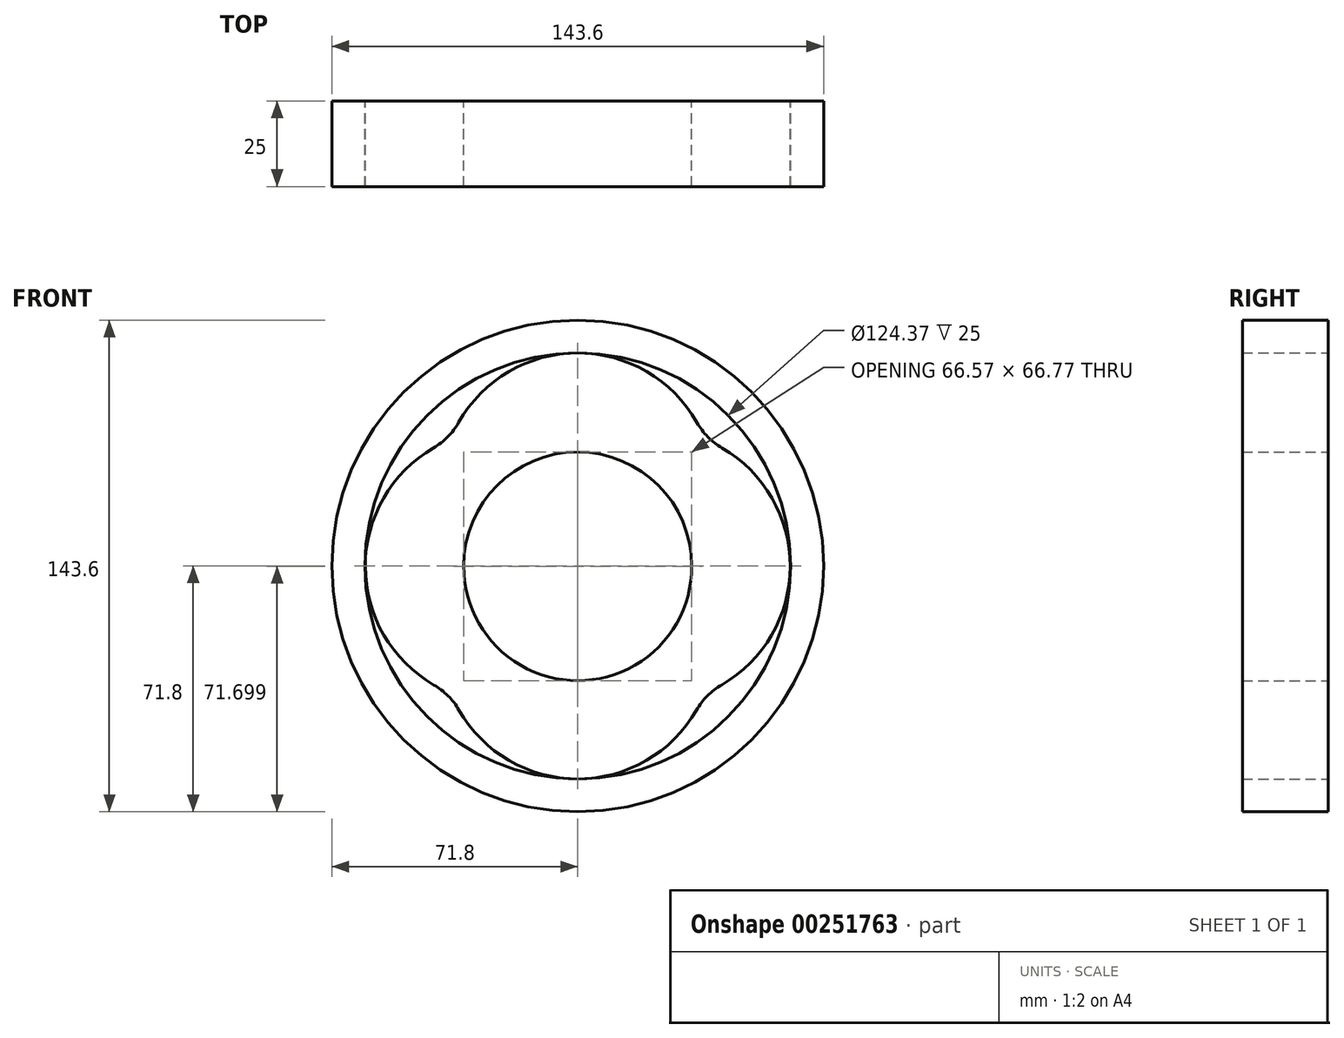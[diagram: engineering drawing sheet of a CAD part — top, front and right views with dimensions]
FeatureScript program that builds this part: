
annotation { "Feature Type Name" : "Feature", "Feature Type Description" : "" }
export const myFeature = defineFeature(function(context is Context, id is Id, definition is map)
    precondition{}
    {
        {
            var Q0;
            Q0=qCreatedBy(makeId("Front.planeOp"),FACE);
            var sketch = newSketch(context, id + "F0", { "sketchPlane" : qUnion([Q0])});
            skArc(sketch, "E0", {"start": v(33.28, 0) * mm, "mid": v(0, 33.28) * mm, "end": v(-33.28, 0) * mm});
            skArc(sketch, "E1", {"start": v(-33.28, 0) * mm, "mid": v(0, -33.49) * mm, "end": v(33.28, 0) * mm});
            skArc(sketch, "E2", {"start": v(33.21, -0.11) * mm, "mid": v(33.21, 0) * mm, "end": v(33.21, 0.11) * mm});
            skArc(sketch, "E3", {"start": v(-32.82, 0.68) * mm, "mid": v(-23.52, -23.23) * mm, "end": v(0, -33.49) * mm});
            skArc(sketch, "E4", {"start": v(33.28, 0) * mm, "mid": v(0, 62.18) * mm, "end": v(-33.28, 0) * mm});
            skArc(sketch, "E5", {"start": v(-33.28, 0) * mm, "mid": v(0, -17.82) * mm, "end": v(33.28, 0) * mm});
            skArc(sketch, "E6", {"start": v(0, -33.49) * mm, "mid": v(62.03, -0.1) * mm, "end": v(0, 33.28) * mm});
            skArc(sketch, "E7", {"start": v(0, 33.28) * mm, "mid": v(-17.97, -0.1) * mm, "end": v(0, -33.49) * mm});
            skArc(sketch, "E8", {"start": v(-33.28, 0) * mm, "mid": v(0, -62.18) * mm, "end": v(33.28, 0) * mm});
            skArc(sketch, "E9", {"start": v(33.28, 0) * mm, "mid": v(0, 17.82) * mm, "end": v(-33.28, 0) * mm});
            skArc(sketch, "E10", {"start": v(0, 33.28) * mm, "mid": v(-62.03, -0.1) * mm, "end": v(0, -33.49) * mm});
            skArc(sketch, "E11", {"start": v(0, -33.49) * mm, "mid": v(17.97, -0.1) * mm, "end": v(0, 33.28) * mm});
            skSolve(sketch);
        }
        {
            var Q0;
            Q0 = qSketchRegion(id + "F0", true);
            extrude(context, id + "F1", {"entities" : qUnion([Q0]), "depth" : 25 * mm});
        }
        {
            var Q0;
            Q0=makeQuery(id+"F1.opExtrude","SWEPT_EDGE",EDGE,{"disambiguationData":[OSD([sQuery(id+"F0.wireOp",EDGE,"E4"),sQuery(id+"F0.wireOp",EDGE,"E10")])]});
            var Q1;
            Q1=makeQuery(id+"F1.opExtrude","SWEPT_EDGE",EDGE,{"disambiguationData":[OSD([sQuery(id+"F0.wireOp",EDGE,"E4"),sQuery(id+"F0.wireOp",EDGE,"E6")])]});
            var Q2;
            Q2=makeQuery(id+"F1.opExtrude","SWEPT_EDGE",EDGE,{"disambiguationData":[OSD([sQuery(id+"F0.wireOp",EDGE,"E6"),sQuery(id+"F0.wireOp",EDGE,"E8")])]});
            var Q3;
            Q3=makeQuery(id+"F1.opExtrude","SWEPT_EDGE",EDGE,{"disambiguationData":[OSD([sQuery(id+"F0.wireOp",EDGE,"E8"),sQuery(id+"F0.wireOp",EDGE,"E10")])]});
            fillet(context, id + "F2", {"entities" : qUnion([Q0, Q1, Q2, Q3]), "radius" : 20 * mm, "tangentPropagation" : true, "allowEdgeOverflow" : false});
        }
        {
            var Q0;
            Q0=qCreatedBy(makeId("Front.planeOp"),FACE);
            var sketch = newSketch(context, id + "F3", { "sketchPlane" : qUnion([Q0])});
            skCircle(sketch, "E12", {"center": v(0, 0) * mm, "radius": 62.18 * mm});
            skCircle(sketch, "E13", {"center": v(0, 0) * mm, "radius": 71.8 * mm});
            skSolve(sketch);
        }
        {
            var Q0;
            Q0 = qSketchRegion(id + "F3", true);
            extrude(context, id + "F4", {"entities" : qUnion([Q0]), "operationType" : NewBodyOperationType.ADD, "depth" : 25 * mm});
        }
    });
